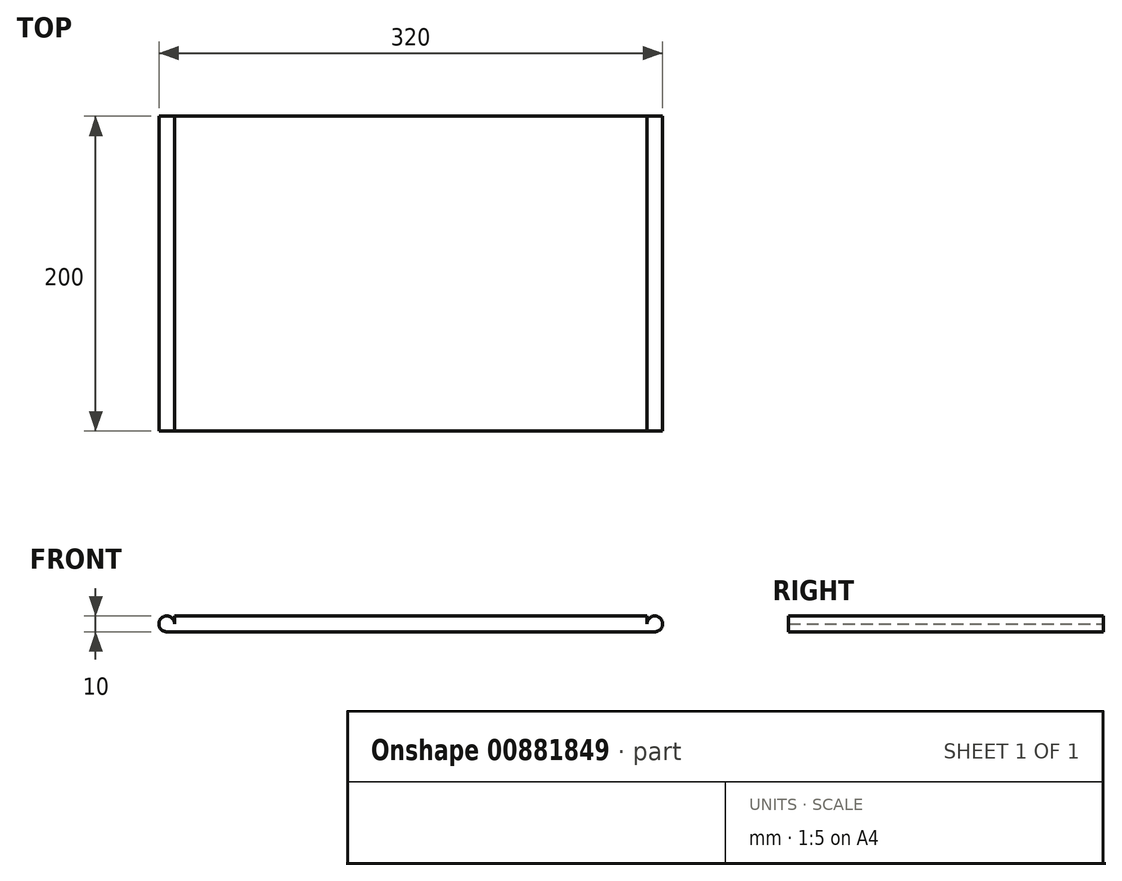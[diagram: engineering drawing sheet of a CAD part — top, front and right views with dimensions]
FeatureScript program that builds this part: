
annotation { "Feature Type Name" : "Feature", "Feature Type Description" : "" }
export const myFeature = defineFeature(function(context is Context, id is Id, definition is map)
    precondition{}
    {
        {
            var Q0;
            Q0=qCreatedBy(makeId("Front.planeOp"),FACE);
            var sketch = newSketch(context, id + "F0", { "sketchPlane" : qUnion([Q0])});
            skLineSegment(sketch, "E0.bottom", {"start": v(155, -5) * mm, "end": v(-155, -5) * mm});
            skLineSegment(sketch, "E0.top", {"start": v(150, 5) * mm, "end": v(-150, 5) * mm});
            skPoint(sketch, "E0.middle", {"position": v(0, 0) * mm});
            skArc(sketch, "E1", {"start": v(155, -5) * mm, "mid": v(158.54, 3.54) * mm, "end": v(150, 0) * mm});
            skArc(sketch, "E2", {"start": v(-150, 0) * mm, "mid": v(-158.54, 3.54) * mm, "end": v(-155, -5) * mm});
            skLineSegment(sketch, "E3", {"start": v(-150, 0) * mm, "end": v(-150, 5) * mm});
            skLineSegment(sketch, "E4", {"start": v(150, 0) * mm, "end": v(150, 5) * mm});
            skPoint(sketch, "E5.orphan", {"position": v(155, 5) * mm});
            skPoint(sketch, "E6.orphan", {"position": v(-155, 5) * mm});
            skSolve(sketch);
        }
        {
            var Q0;
            Q0=makeQuery(id+"F0.imprint","IMPRINT",FACE,{"disambiguationData":[TD([[makeQuery(id+"F0.imprint","IMPRINT",EDGE,{"derivedFrom":sQuery(id+"F0.wireOp",EDGE,"E0.bottom")}),-1.0]])]});
            extrude(context, id + "F1", {"entities" : qUnion([Q0]), "endBound" : BoundingType.SYMMETRIC, "depth" : 200 * mm, "offsetDistance" : 25.4 * mm});
        }
    });
